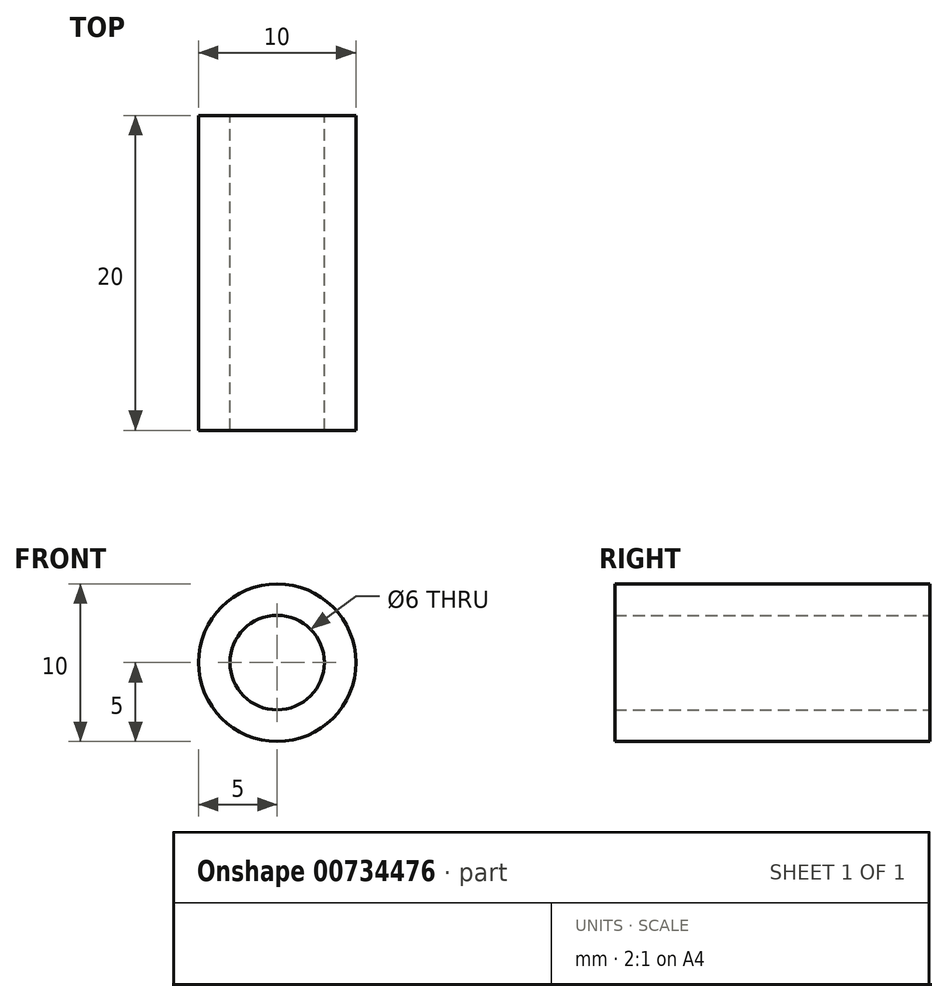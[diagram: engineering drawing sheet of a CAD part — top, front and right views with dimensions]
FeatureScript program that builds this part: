
annotation { "Feature Type Name" : "Feature", "Feature Type Description" : "" }
export const myFeature = defineFeature(function(context is Context, id is Id, definition is map)
    precondition{}
    {
        {
            var Q0;
            Q0=qCreatedBy(makeId("Front.planeOp"),FACE);
            var sketch = newSketch(context, id + "F0", { "sketchPlane" : qUnion([Q0])});
            skCircle(sketch, "E0", {"center": v(0, 0) * mm, "radius": 5 * mm});
            skCircle(sketch, "E1", {"center": v(0, 0) * mm, "radius": 3 * mm});
            skSolve(sketch);
        }
        {
            var Q0;
            Q0 = qSketchRegion(id + "F0", true);
            extrude(context, id + "F1", {"entities" : qUnion([Q0]), "depth" : 20 * mm, "offsetDistance" : 25 * mm});
        }
    });
